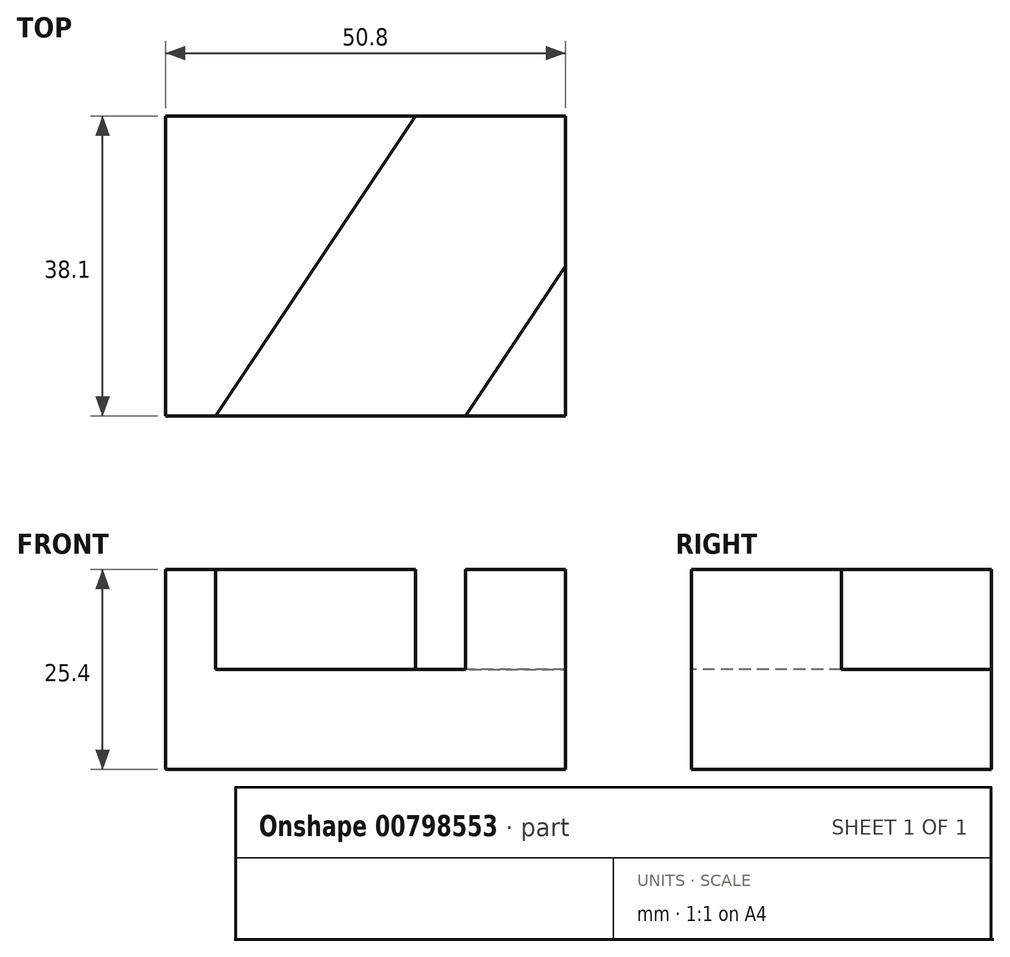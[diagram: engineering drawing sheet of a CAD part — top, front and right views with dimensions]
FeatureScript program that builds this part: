
annotation { "Feature Type Name" : "Feature", "Feature Type Description" : "" }
export const myFeature = defineFeature(function(context is Context, id is Id, definition is map)
    precondition{}
    {
        {
            var Q0;
            Q0=qCreatedBy(makeId("Front.planeOp"),FACE);
            var sketch = newSketch(context, id + "F0", { "sketchPlane" : qUnion([Q0])});
            skLineSegment(sketch, "E0", {"start": v(0, 0) * mm, "end": v(50.8, 0) * mm});
            skLineSegment(sketch, "E1", {"start": v(50.8, 0) * mm, "end": v(50.8, 25.4) * mm});
            skLineSegment(sketch, "E2", {"start": v(50.8, 25.4) * mm, "end": v(38.1, 25.4) * mm});
            skLineSegment(sketch, "E3", {"start": v(38.1, 25.4) * mm, "end": v(38.1, 12.7) * mm});
            skLineSegment(sketch, "E4", {"start": v(0, 0) * mm, "end": v(0, 25.4) * mm});
            skLineSegment(sketch, "E5", {"start": v(0, 25.4) * mm, "end": v(6.35, 25.4) * mm});
            skLineSegment(sketch, "E6", {"start": v(6.35, 25.4) * mm, "end": v(6.35, 12.7) * mm});
            skLineSegment(sketch, "E7", {"start": v(6.35, 12.7) * mm, "end": v(38.1, 12.7) * mm});
            skSolve(sketch);
        }
        {
            var Q0;
            Q0=makeQuery(id+"F0.imprint","IMPRINT",FACE,{"disambiguationData":[TD([[makeQuery(id+"F0.imprint","IMPRINT",EDGE,{"derivedFrom":sQuery(id+"F0.wireOp",EDGE,"E0")}),1.0]])]});
            extrude(context, id + "F1", {"entities" : qUnion([Q0]), "depth" : 38.1 * mm, "offsetDistance" : 25.4 * mm});
        }
        {
            var Q0;
            Q0=makeQuery(id+"F1.opExtrude","SWEPT_FACE",FACE,{"disambiguationData":[OSD([sQuery(id+"F0.wireOp",EDGE,"E2")])]});
            var sketch = newSketch(context, id + "F2", { "sketchPlane" : qUnion([Q0])});
            skLineSegment(sketch, "E8", {"start": v(50.8, -38.1) * mm, "end": v(50.8, -19.05) * mm});
            skLineSegment(sketch, "E9", {"start": v(50.8, -19.05) * mm, "end": v(38.1, -38.1) * mm});
            skSolve(sketch);
        }
        {
            var Q0;
            {var subQ0=sQuery(id+"F2.wireOp",EDGE,"E9");Q0=makeQuery(id+"F2.imprint","IMPRINT",FACE,{"disambiguationData":[TD([[makeQuery(id+"F2.imprint","IMPRINT",EDGE,{"derivedFrom":subQ0}),-1.0]])]});}
            extrude(context, id + "F3", {"entities" : qUnion([Q0]), "operationType" : NewBodyOperationType.REMOVE, "oppositeDirection" : true, "depth" : 12.7 * mm, "offsetDistance" : 25.4 * mm});
        }
        {
            var Q0;
            Q0=makeQuery(id+"F1.opExtrude","SWEPT_FACE",FACE,{"disambiguationData":[OSD([sQuery(id+"F0.wireOp",EDGE,"E5")])]});
            var sketch = newSketch(context, id + "F4", { "sketchPlane" : qUnion([Q0])});
            skLineSegment(sketch, "E10", {"start": v(0, 0) * mm, "end": v(31.75, 0) * mm});
            skLineSegment(sketch, "E11", {"start": v(0, -38.1) * mm, "end": v(6.35, -38.1) * mm});
            skLineSegment(sketch, "E12", {"start": v(31.75, 0) * mm, "end": v(6.35, -38.1) * mm});
            skSolve(sketch);
        }
        {
            var Q0;
            {var subQ2=sQuery(id+"F4.wireOp",EDGE,"E12");Q0=makeQuery(id+"F4.imprint","IMPRINT",FACE,{"disambiguationData":[TD([[makeQuery(id+"F4.imprint","IMPRINT",EDGE,{"derivedFrom":subQ2}),-1.0]])]});}
            extrude(context, id + "F5", {"entities" : qUnion([Q0]), "operationType" : NewBodyOperationType.ADD, "oppositeDirection" : true, "depth" : 12.7 * mm, "offsetDistance" : 25.4 * mm});
        }
    });
